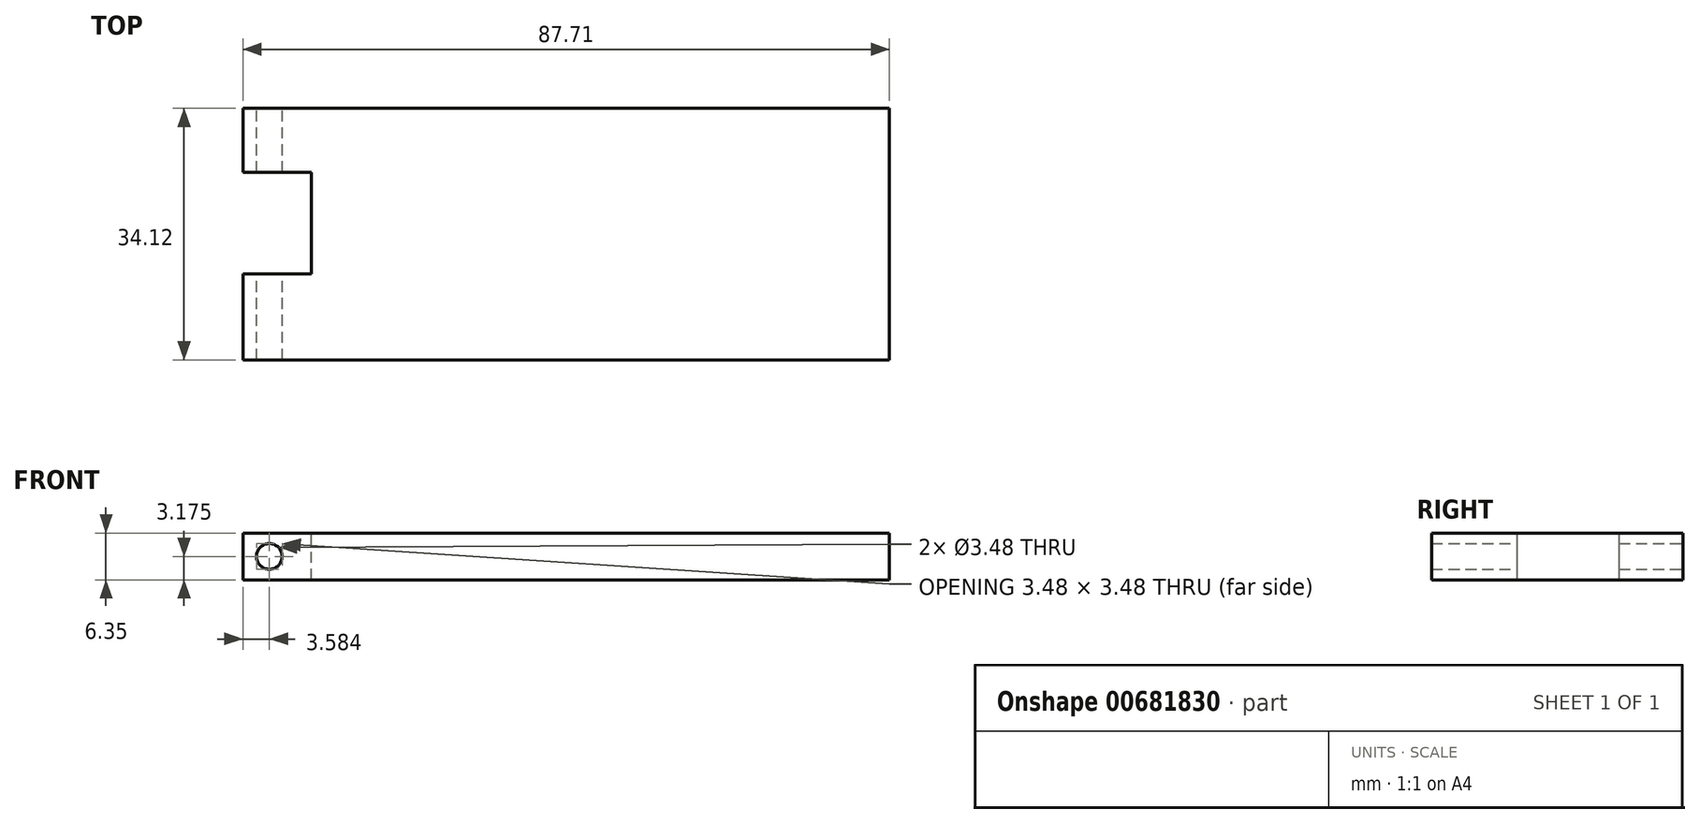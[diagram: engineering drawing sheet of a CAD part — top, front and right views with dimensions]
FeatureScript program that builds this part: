
annotation { "Feature Type Name" : "Feature", "Feature Type Description" : "" }
export const myFeature = defineFeature(function(context is Context, id is Id, definition is map)
    precondition{}
    {
        {
            var Q0;
            Q0=qCreatedBy(makeId("Top.planeOp"),FACE);
            var sketch = newSketch(context, id + "F0", { "sketchPlane" : qUnion([Q0])});
            skLineSegment(sketch, "E0.bottom", {"start": v(0, 0) * mm, "end": v(87.7, 0) * mm});
            skLineSegment(sketch, "E0.top", {"start": v(0, 34.12) * mm, "end": v(87.7, 34.12) * mm});
            skLineSegment(sketch, "E0.left", {"start": v(0, 0) * mm, "end": v(0, 34.12) * mm});
            skLineSegment(sketch, "E0.right", {"start": v(87.7, 0) * mm, "end": v(87.7, 34.12) * mm});
            skSolve(sketch);
        }
        {
            var Q0;
            Q0 = qSketchRegion(id + "F0", true);
            extrude(context, id + "F1", {"entities" : qUnion([Q0]), "depth" : 6.35 * mm, "offsetDistance" : 25.4 * mm});
        }
        {
            var Q0;
            Q0=makeQuery(id+"F1.opExtrude","CAP_FACE",FACE,{"disambiguationData":[OSD([sQuery(id+"F0.wireOp",EDGE,"E0.bottom"),sQuery(id+"F0.wireOp",EDGE,"E0.top"),sQuery(id+"F0.wireOp",EDGE,"E0.left"),sQuery(id+"F0.wireOp",EDGE,"E0.right")])],"isStart":false});
            var sketch = newSketch(context, id + "F2", { "sketchPlane" : qUnion([Q0])});
            skLineSegment(sketch, "E1.bottom", {"start": v(0, 11.65) * mm, "end": v(9.31, 11.65) * mm});
            skLineSegment(sketch, "E1.top", {"start": v(0, 25.45) * mm, "end": v(9.31, 25.45) * mm});
            skLineSegment(sketch, "E1.left", {"start": v(0, 11.65) * mm, "end": v(0, 25.45) * mm});
            skLineSegment(sketch, "E1.right", {"start": v(9.31, 11.65) * mm, "end": v(9.31, 25.45) * mm});
            skSolve(sketch);
        }
        {
            var Q0;
            Q0 = qSketchRegion(id + "F2", true);
            var Q1;
            Q1=makeQuery(id+"F1.opExtrude","CAP_FACE",FACE,{"disambiguationData":[OSD([sQuery(id+"F0.wireOp",EDGE,"E0.bottom"),sQuery(id+"F0.wireOp",EDGE,"E0.top"),sQuery(id+"F0.wireOp",EDGE,"E0.left"),sQuery(id+"F0.wireOp",EDGE,"E0.right")])],"isStart":true});
            extrude(context, id + "F3", {"entities" : qUnion([Q0]), "operationType" : NewBodyOperationType.REMOVE, "endBound" : BoundingType.UP_TO_SURFACE, "oppositeDirection" : true, "depth" : 25.4 * mm, "endBoundEntityFace" : qUnion([Q1]), "offsetDistance" : 25.4 * mm});
        }
        {
            var Q0;
            Q0=makeQuery(id+"F1.opExtrude","SWEPT_FACE",FACE,{"disambiguationData":[OSD([sQuery(id+"F0.wireOp",EDGE,"E0.top")])]});
            var sketch = newSketch(context, id + "F4", { "sketchPlane" : qUnion([Q0])});
            skCircle(sketch, "E2", {"center": v(-3.58, 3.18) * mm, "radius": 1.74 * mm});
            skPoint(sketch, "E2.centerSnap0", {"position": v(0, 3.18) * mm});
            skSolve(sketch);
        }
        {
            var Q0;
            Q0=makeQuery(id+"F4.imprint","IMPRINT",FACE,{"disambiguationData":[TD([[makeQuery(id+"F4.imprint","IMPRINT",EDGE,{"derivedFrom":sQuery(id+"F4.wireOp",EDGE,"E2")}),1.0]])]});
            var Q1;
            Q1=makeQuery(id+"F1.opExtrude","SWEPT_FACE",FACE,{"disambiguationData":[OSD([sQuery(id+"F0.wireOp",EDGE,"E0.bottom")])]});
            extrude(context, id + "F5", {"entities" : qUnion([Q0]), "operationType" : NewBodyOperationType.REMOVE, "endBound" : BoundingType.UP_TO_SURFACE, "oppositeDirection" : true, "depth" : 25.4 * mm, "endBoundEntityFace" : qUnion([Q1]), "offsetDistance" : 25.4 * mm});
        }
    });
